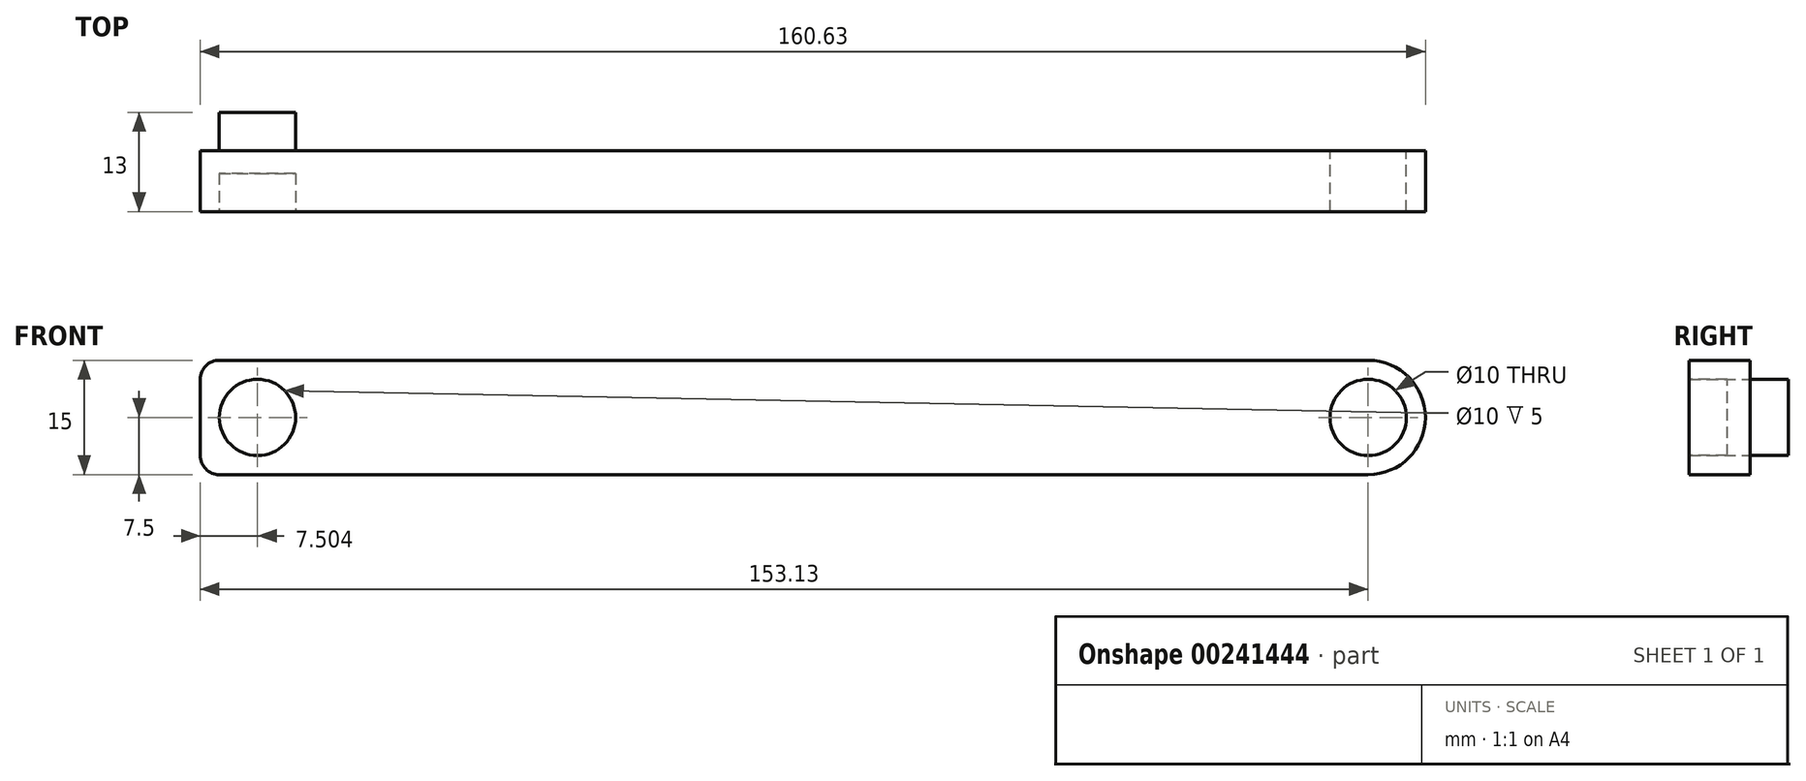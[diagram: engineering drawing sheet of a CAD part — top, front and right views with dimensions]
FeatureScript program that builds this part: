
annotation { "Feature Type Name" : "Feature", "Feature Type Description" : "" }
export const myFeature = defineFeature(function(context is Context, id is Id, definition is map)
    precondition{}
    {
        {
            var Q0;
            Q0=qCreatedBy(makeId("Front.planeOp"),FACE);
            var sketch = newSketch(context, id + "F0", { "sketchPlane" : qUnion([Q0])});
            skCircle(sketch, "E0", {"center": v(0, 0) * mm, "radius": 7.5 * mm});
            skCircle(sketch, "E1", {"center": v(0, 0) * mm, "radius": 5 * mm});
            skLineSegment(sketch, "E2.bottom", {"start": v(0, 7.5) * mm, "end": v(-153.13, 7.5) * mm});
            skLineSegment(sketch, "E2.top", {"start": v(0, -7.5) * mm, "end": v(-153.13, -7.5) * mm});
            skLineSegment(sketch, "E2.left", {"start": v(0, 7.5) * mm, "end": v(0, -7.5) * mm});
            skLineSegment(sketch, "E2.right", {"start": v(-153.13, 7.5) * mm, "end": v(-153.13, -7.5) * mm});
            skSolve(sketch);
        }
        {
            var Q0;
            {var subQ1=sQuery(id+"F0.wireOp",EDGE,"NwCUDoeX-6FFx-rpG8-aocx-gNc1TtZu7neD");Q0=makeQuery(id+"F0.imprint","IMPRINT",FACE,{"disambiguationData":[TD([[makeQuery(id+"F0.imprint","IMPRINT",EDGE,{"derivedFrom":subQ1}),-1.0]])]});}
            var Q1;
            {var subQ0=sQuery(id+"F0.wireOp",EDGE,"pMUDdTaR-RGpa-3EbT-v0LG-Nu6DOzsx8AzA");var subQ4=sQuery(id+"F0.wireOp",EDGE,"IL5Tp1Po-sgq1-uV5f-WThu-FCOuGZ4YDNK1");var subQ5=makeQuery(id+"F0.imprint","INTERSECT",VERTEX,{"disambiguationData":[OD(0.0)],"derivedFrom":[subQ4,subQ0]});Q1=makeQuery(id+"F0.imprint","IMPRINT",FACE,{"disambiguationData":[TD([[makeQuery(id+"F0.imprint","IMPRINT",EDGE,{"disambiguationData":[TD([[subQ5,-1.0]])],"derivedFrom":subQ4}),-1.0]])]});}
            var Q2;
            {var subQ0=sQuery(id+"F0.wireOp",EDGE,"pMUDdTaR-RGpa-3EbT-v0LG-Nu6DOzsx8AzA");var subQ4=sQuery(id+"F0.wireOp",EDGE,"IL5Tp1Po-sgq1-uV5f-WThu-FCOuGZ4YDNK1");var subQ5=makeQuery(id+"F0.imprint","INTERSECT",VERTEX,{"disambiguationData":[OD(0.0)],"derivedFrom":[subQ4,subQ0]});Q2=makeQuery(id+"F0.imprint","IMPRINT",FACE,{"disambiguationData":[TD([[makeQuery(id+"F0.imprint","IMPRINT",EDGE,{"disambiguationData":[TD([[subQ5,1.0]])],"derivedFrom":subQ4}),-1.0]])]});}
            var Q3;
            {var subQ1=sQuery(id+"F0.wireOp",EDGE,"E2.bottom");Q3=makeQuery(id+"F0.imprint","IMPRINT",FACE,{"disambiguationData":[TD([[makeQuery(id+"F0.imprint","IMPRINT",EDGE,{"derivedFrom":subQ1}),1.0]])]});}
            var Q4;
            {var subQ0=sQuery(id+"F0.wireOp",EDGE,"E2.left");var subQ4=sQuery(id+"F0.wireOp",EDGE,"E1");var subQ5=makeQuery(id+"F0.imprint","INTERSECT",VERTEX,{"disambiguationData":[OD(0.0)],"derivedFrom":[subQ4,subQ0]});Q4=makeQuery(id+"F0.imprint","IMPRINT",FACE,{"disambiguationData":[TD([[makeQuery(id+"F0.imprint","IMPRINT",EDGE,{"disambiguationData":[TD([[subQ5,-1.0]])],"derivedFrom":subQ4}),-1.0]])]});}
            var Q5;
            {var subQ0=sQuery(id+"F0.wireOp",EDGE,"E2.left");var subQ4=sQuery(id+"F0.wireOp",EDGE,"E1");var subQ5=makeQuery(id+"F0.imprint","INTERSECT",VERTEX,{"disambiguationData":[OD(0.0)],"derivedFrom":[subQ4,subQ0]});Q5=makeQuery(id+"F0.imprint","IMPRINT",FACE,{"disambiguationData":[TD([[makeQuery(id+"F0.imprint","IMPRINT",EDGE,{"disambiguationData":[TD([[subQ5,1.0]])],"derivedFrom":subQ4}),-1.0]])]});}
            extrude(context, id + "F1", {"entities" : qUnion([Q0, Q1, Q2, Q3, Q4, Q5]), "depth" : 8 * mm});
        }
        {
            var Q0;
            Q0=makeQuery(id+"F1.opExtrude","SWEPT_EDGE",EDGE,{"disambiguationData":[OSD([sQuery(id+"F0.wireOp",EDGE,"E2.bottom"),sQuery(id+"F0.wireOp",EDGE,"E2.right")])]});
            var Q1;
            Q1=makeQuery(id+"F1.opExtrude","SWEPT_EDGE",EDGE,{"disambiguationData":[OSD([sQuery(id+"F0.wireOp",EDGE,"E2.top"),sQuery(id+"F0.wireOp",EDGE,"E2.right")])]});
            fillet(context, id + "F2", {"entities" : qUnion([Q0, Q1]), "radius" : 2.5 * mm, "tangentPropagation" : true, "allowEdgeOverflow" : false});
        }
        {
            var Q0;
            Q0=makeQuery(id+"F1.opExtrude","CAP_FACE",FACE,{"disambiguationData":[OSD([sQuery(id+"F0.wireOp",EDGE,"E0"),sQuery(id+"F0.wireOp",EDGE,"E1"),sQuery(id+"F0.wireOp",EDGE,"E2.bottom"),sQuery(id+"F0.wireOp",EDGE,"E2.top"),sQuery(id+"F0.wireOp",EDGE,"E2.right")])],"isStart":true});
            var sketch = newSketch(context, id + "F3", { "sketchPlane" : qUnion([Q0])});
            skCircle(sketch, "E3", {"center": v(145.63, 0) * mm, "radius": 5 * mm});
            skSolve(sketch);
        }
        {
            var Q0;
            Q0 = qSketchRegion(id + "F3", true);
            extrude(context, id + "F4", {"entities" : qUnion([Q0]), "operationType" : NewBodyOperationType.ADD, "depth" : 5 * mm});
        }
        {
            var Q0;
            Q0=makeQuery(id+"F1.opExtrude","CAP_FACE",FACE,{"disambiguationData":[OSD([sQuery(id+"F0.wireOp",EDGE,"E0"),sQuery(id+"F0.wireOp",EDGE,"E1"),sQuery(id+"F0.wireOp",EDGE,"E2.bottom"),sQuery(id+"F0.wireOp",EDGE,"E2.top"),sQuery(id+"F0.wireOp",EDGE,"E2.right")])],"isStart":false});
            var sketch = newSketch(context, id + "F5", { "sketchPlane" : qUnion([Q0])});
            skCircle(sketch, "E4", {"center": v(-145.63, 0) * mm, "radius": 5 * mm});
            skSolve(sketch);
        }
        {
            var Q0;
            Q0 = qSketchRegion(id + "F5", true);
            extrude(context, id + "F6", {"entities" : qUnion([Q0]), "operationType" : NewBodyOperationType.REMOVE, "oppositeDirection" : true, "depth" : 5 * mm});
        }
    });
